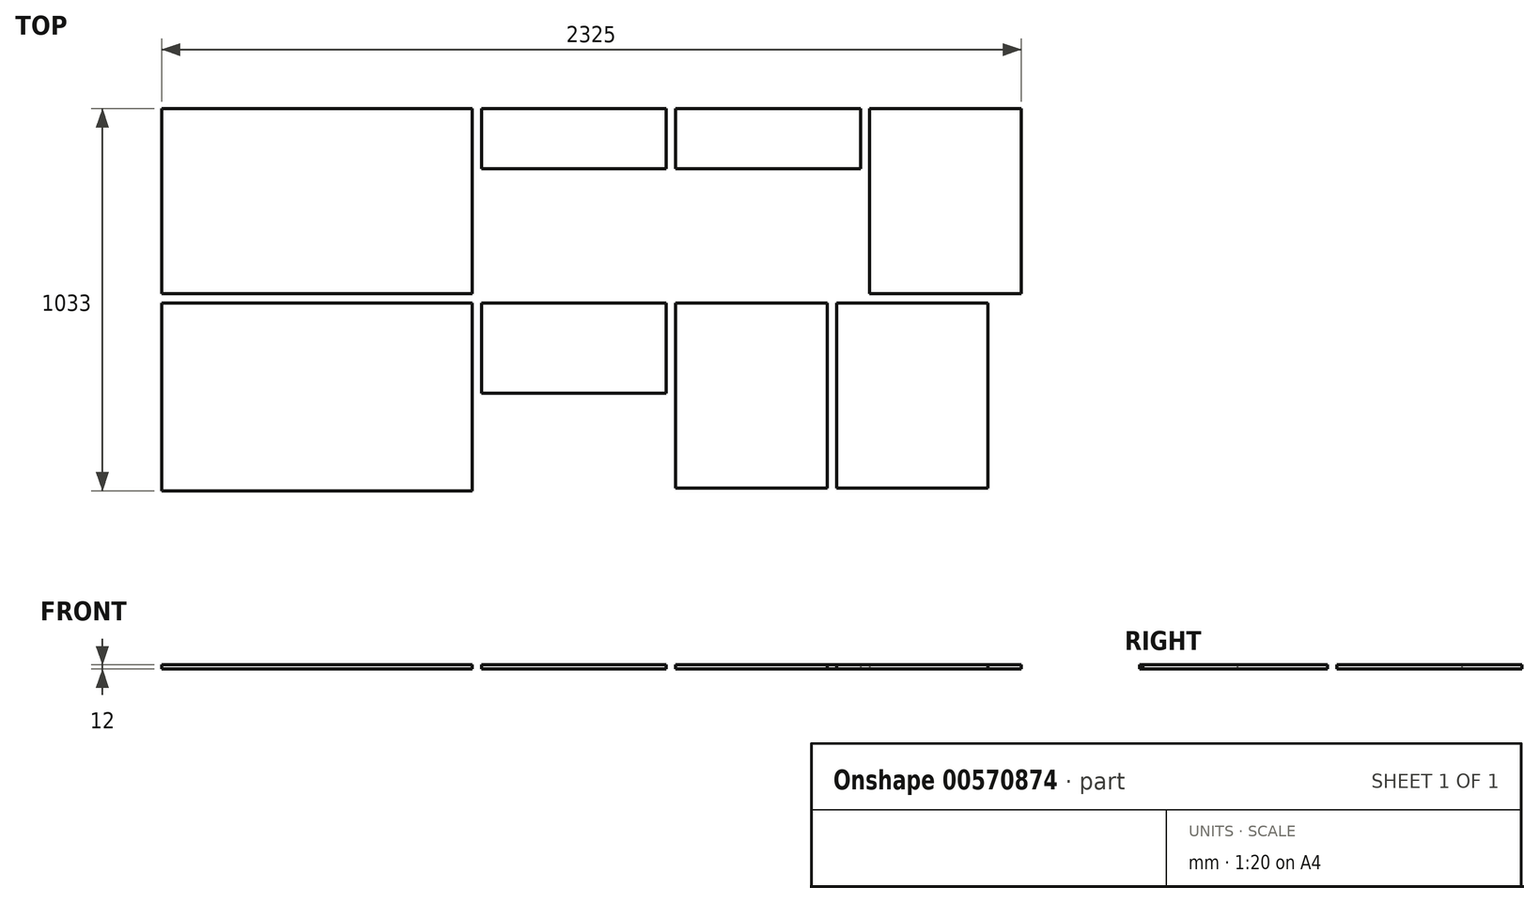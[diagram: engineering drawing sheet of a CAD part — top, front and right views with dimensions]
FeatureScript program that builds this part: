
annotation { "Feature Type Name" : "Feature", "Feature Type Description" : "" }
export const myFeature = defineFeature(function(context is Context, id is Id, definition is map)
    precondition{}
    {
        {
            var Q0;
            Q0=qCreatedBy(makeId("Top.planeOp"),FACE);
            var sketch = newSketch(context, id + "F0", { "sketchPlane" : qUnion([Q0])});
            skLineSegment(sketch, "E0.bottom", {"start": v(-1371.68, 213.83) * mm, "end": v(1058.32, 213.83) * mm});
            skLineSegment(sketch, "E0.top", {"start": v(-1371.68, -1001.17) * mm, "end": v(1058.32, -1001.17) * mm});
            skLineSegment(sketch, "E0.left", {"start": v(-1371.68, 213.83) * mm, "end": v(-1371.68, -1001.17) * mm});
            skLineSegment(sketch, "E0.right", {"start": v(1058.32, 213.83) * mm, "end": v(1058.32, -1001.17) * mm});
            skLineSegment(sketch, "E1.bottom", {"start": v(-1346.68, 188.83) * mm, "end": v(-506.68, 188.83) * mm});
            skLineSegment(sketch, "E1.top", {"start": v(-1346.68, -311.17) * mm, "end": v(-506.68, -311.17) * mm});
            skLineSegment(sketch, "E1.left", {"start": v(-1346.68, 188.83) * mm, "end": v(-1346.68, -311.17) * mm});
            skLineSegment(sketch, "E1.right", {"start": v(-506.68, 188.83) * mm, "end": v(-506.68, -311.17) * mm});
            skLineSegment(sketch, "E2.bottom", {"start": v(-1346.68, -336.17) * mm, "end": v(-506.68, -336.17) * mm});
            skLineSegment(sketch, "E2.top", {"start": v(-1346.68, -844.17) * mm, "end": v(-506.68, -844.17) * mm});
            skLineSegment(sketch, "E2.left", {"start": v(-1346.68, -336.17) * mm, "end": v(-1346.68, -844.17) * mm});
            skLineSegment(sketch, "E2.right", {"start": v(-506.68, -336.17) * mm, "end": v(-506.68, -844.17) * mm});
            skLineSegment(sketch, "E3.bottom", {"start": v(-481.68, 188.83) * mm, "end": v(18.32, 188.83) * mm});
            skLineSegment(sketch, "E3.top", {"start": v(-481.68, -311.17) * mm, "end": v(18.32, -311.17) * mm});
            skLineSegment(sketch, "E3.left", {"start": v(-481.68, 188.83) * mm, "end": v(-481.68, -311.17) * mm});
            skLineSegment(sketch, "E3.right", {"start": v(18.32, 188.83) * mm, "end": v(18.32, -311.17) * mm});
            skLineSegment(sketch, "E4.bottom", {"start": v(43.32, 188.83) * mm, "end": v(543.32, 188.83) * mm});
            skLineSegment(sketch, "E4.top", {"start": v(43.32, -311.17) * mm, "end": v(543.32, -311.17) * mm});
            skLineSegment(sketch, "E4.left", {"start": v(43.32, 188.83) * mm, "end": v(43.32, -311.17) * mm});
            skLineSegment(sketch, "E4.right", {"start": v(543.32, 188.83) * mm, "end": v(543.32, -311.17) * mm});
            skLineSegment(sketch, "E5.bottom", {"start": v(-481.68, -336.17) * mm, "end": v(18.32, -336.17) * mm});
            skLineSegment(sketch, "E5.top", {"start": v(-481.68, -836.17) * mm, "end": v(18.32, -836.17) * mm});
            skLineSegment(sketch, "E5.left", {"start": v(-481.68, -336.17) * mm, "end": v(-481.68, -836.17) * mm});
            skLineSegment(sketch, "E5.right", {"start": v(18.32, -336.17) * mm, "end": v(18.32, -836.17) * mm});
            skLineSegment(sketch, "E6.bottom", {"start": v(568.32, 188.83) * mm, "end": v(978.32, 188.83) * mm});
            skLineSegment(sketch, "E6.top", {"start": v(568.32, -311.17) * mm, "end": v(978.32, -311.17) * mm});
            skLineSegment(sketch, "E6.left", {"start": v(568.32, 188.83) * mm, "end": v(568.32, -311.17) * mm});
            skLineSegment(sketch, "E6.right", {"start": v(978.32, 188.83) * mm, "end": v(978.32, -311.17) * mm});
            skLineSegment(sketch, "E7.bottom", {"start": v(43.32, -336.17) * mm, "end": v(453.32, -336.17) * mm});
            skLineSegment(sketch, "E7.top", {"start": v(43.32, -836.17) * mm, "end": v(453.32, -836.17) * mm});
            skLineSegment(sketch, "E7.left", {"start": v(43.32, -336.17) * mm, "end": v(43.32, -836.17) * mm});
            skLineSegment(sketch, "E7.right", {"start": v(453.32, -336.17) * mm, "end": v(453.32, -836.17) * mm});
            skLineSegment(sketch, "E8.bottom", {"start": v(478.32, -336.17) * mm, "end": v(888.32, -336.17) * mm});
            skLineSegment(sketch, "E8.top", {"start": v(478.32, -836.17) * mm, "end": v(888.32, -836.17) * mm});
            skLineSegment(sketch, "E8.left", {"start": v(478.32, -336.17) * mm, "end": v(478.32, -836.17) * mm});
            skLineSegment(sketch, "E8.right", {"start": v(888.32, -336.17) * mm, "end": v(888.32, -836.17) * mm});
            skLineSegment(sketch, "E9", {"start": v(-1334.68, 188.83) * mm, "end": v(-1334.68, -311.17) * mm});
            skLineSegment(sketch, "E10", {"start": v(-518.68, 188.83) * mm, "end": v(-518.68, -311.17) * mm});
            skLineSegment(sketch, "E11.bottom", {"start": v(-932.68, 188.83) * mm, "end": v(-920.68, 188.83) * mm});
            skLineSegment(sketch, "E11.top", {"start": v(-932.68, -311.17) * mm, "end": v(-920.68, -311.17) * mm});
            skLineSegment(sketch, "E11.left", {"start": v(-932.68, 188.83) * mm, "end": v(-932.68, -311.17) * mm});
            skLineSegment(sketch, "E11.right", {"start": v(-920.68, 188.83) * mm, "end": v(-920.68, -311.17) * mm});
            skLineSegment(sketch, "E12.bottom", {"start": v(-481.68, -154.17) * mm, "end": v(18.32, -154.17) * mm});
            skLineSegment(sketch, "E12.top", {"start": v(-481.68, -142.17) * mm, "end": v(18.32, -142.17) * mm});
            skLineSegment(sketch, "E12.left", {"start": v(-481.68, -154.17) * mm, "end": v(-481.68, -142.17) * mm});
            skLineSegment(sketch, "E12.right", {"start": v(18.32, -154.17) * mm, "end": v(18.32, -142.17) * mm});
            skLineSegment(sketch, "E13.bottom", {"start": v(-481.68, 26.83) * mm, "end": v(18.32, 26.83) * mm});
            skLineSegment(sketch, "E13.top", {"start": v(-481.68, 14.83) * mm, "end": v(18.32, 14.83) * mm});
            skLineSegment(sketch, "E13.left", {"start": v(-481.68, 26.83) * mm, "end": v(-481.68, 14.83) * mm});
            skLineSegment(sketch, "E13.right", {"start": v(18.32, 26.83) * mm, "end": v(18.32, 14.83) * mm});
            skLineSegment(sketch, "E14.bottom", {"start": v(43.32, 26.83) * mm, "end": v(543.32, 26.83) * mm});
            skLineSegment(sketch, "E14.top", {"start": v(43.32, 14.83) * mm, "end": v(543.32, 14.83) * mm});
            skLineSegment(sketch, "E14.left", {"start": v(43.32, 26.83) * mm, "end": v(43.32, 14.83) * mm});
            skLineSegment(sketch, "E14.right", {"start": v(543.32, 26.83) * mm, "end": v(543.32, 14.83) * mm});
            skLineSegment(sketch, "E15.bottom", {"start": v(43.32, -154.17) * mm, "end": v(543.32, -154.17) * mm});
            skLineSegment(sketch, "E15.top", {"start": v(43.32, -142.17) * mm, "end": v(543.32, -142.17) * mm});
            skLineSegment(sketch, "E15.left", {"start": v(43.32, -154.17) * mm, "end": v(43.32, -142.17) * mm});
            skLineSegment(sketch, "E15.right", {"start": v(543.32, -154.17) * mm, "end": v(543.32, -142.17) * mm});
            skLineSegment(sketch, "E16.bottom", {"start": v(-481.68, -580.17) * mm, "end": v(18.32, -580.17) * mm});
            skLineSegment(sketch, "E16.top", {"start": v(-481.68, -592.17) * mm, "end": v(18.32, -592.17) * mm});
            skLineSegment(sketch, "E16.left", {"start": v(-481.68, -580.17) * mm, "end": v(-481.68, -592.17) * mm});
            skLineSegment(sketch, "E16.right", {"start": v(18.32, -580.17) * mm, "end": v(18.32, -592.17) * mm});
            skSolve(sketch);
        }
        {
            var Q0;
            Q0=makeQuery(id+"F0.imprint","IMPRINT",FACE,{"disambiguationData":[TD([[makeQuery(id+"F0.imprint","IMPRINT",EDGE,{"derivedFrom":sQuery(id+"F0.wireOp",EDGE,"E1.bottom")}),-1.0]])]});
            var Q1;
            Q1=makeQuery(id+"F0.imprint","IMPRINT",FACE,{"disambiguationData":[TD([[makeQuery(id+"F0.imprint","IMPRINT",EDGE,{"derivedFrom":sQuery(id+"F0.wireOp",EDGE,"E2.bottom")}),-1.0]])]});
            var Q2;
            Q2=makeQuery(id+"F0.imprint","IMPRINT",FACE,{"disambiguationData":[TD([[makeQuery(id+"F0.imprint","IMPRINT",EDGE,{"derivedFrom":sQuery(id+"F0.wireOp",EDGE,"E3.bottom")}),-1.0]])]});
            var Q3;
            Q3=makeQuery(id+"F0.imprint","IMPRINT",FACE,{"disambiguationData":[TD([[makeQuery(id+"F0.imprint","IMPRINT",EDGE,{"derivedFrom":sQuery(id+"F0.wireOp",EDGE,"E5.bottom")}),-1.0]])]});
            var Q4;
            Q4=makeQuery(id+"F0.imprint","IMPRINT",FACE,{"disambiguationData":[TD([[makeQuery(id+"F0.imprint","IMPRINT",EDGE,{"derivedFrom":sQuery(id+"F0.wireOp",EDGE,"E7.bottom")}),-1.0]])]});
            var Q5;
            Q5=makeQuery(id+"F0.imprint","IMPRINT",FACE,{"disambiguationData":[TD([[makeQuery(id+"F0.imprint","IMPRINT",EDGE,{"derivedFrom":sQuery(id+"F0.wireOp",EDGE,"E4.bottom")}),-1.0]])]});
            var Q6;
            Q6=makeQuery(id+"F0.imprint","IMPRINT",FACE,{"disambiguationData":[TD([[makeQuery(id+"F0.imprint","IMPRINT",EDGE,{"derivedFrom":sQuery(id+"F0.wireOp",EDGE,"E8.bottom")}),-1.0]])]});
            var Q7;
            Q7=makeQuery(id+"F0.imprint","IMPRINT",FACE,{"disambiguationData":[TD([[makeQuery(id+"F0.imprint","IMPRINT",EDGE,{"derivedFrom":sQuery(id+"F0.wireOp",EDGE,"E6.bottom")}),-1.0]])]});
            var Q8;
            Q8=makeQuery(id+"F0.imprint","IMPRINT",FACE,{"disambiguationData":[TD([[makeQuery(id+"F0.imprint","IMPRINT",EDGE,{"derivedFrom":sQuery(id+"F0.wireOp",EDGE,"mVEvi2md-ZAMZ-gTHu-SLhE-P8r4IFi62GfL.bottom")}),-1.0]])]});
            extrude(context, id + "F1", {"entities" : qUnion([Q0, Q1, Q2, Q3, Q4, Q5, Q6, Q7, Q8]), "depth" : 12 * mm, "offsetDistance" : 25 * mm});
        }
    });
